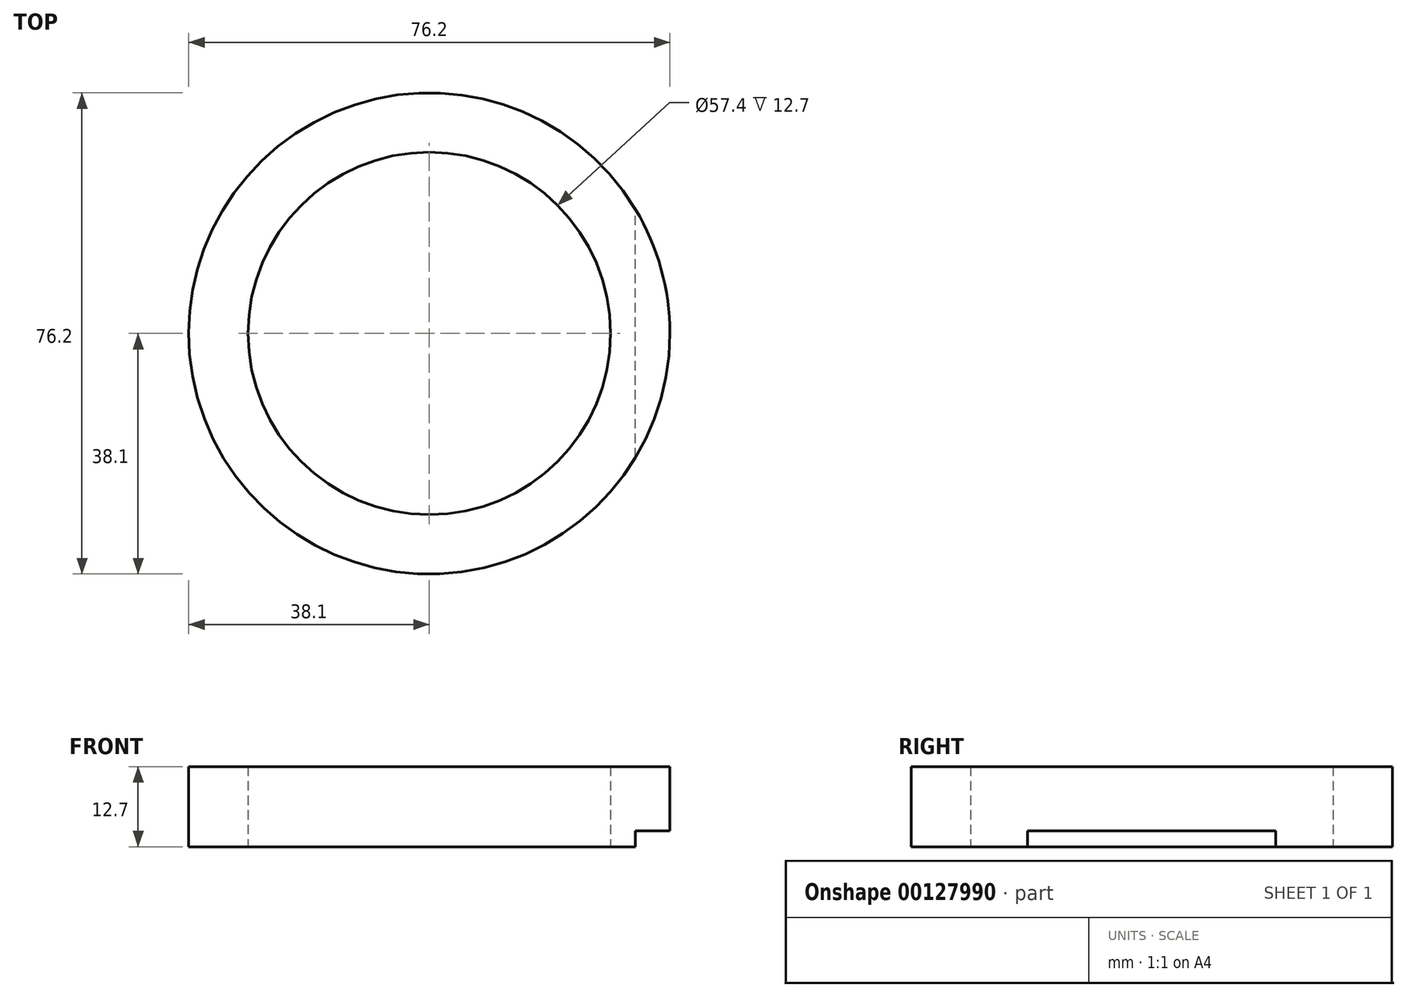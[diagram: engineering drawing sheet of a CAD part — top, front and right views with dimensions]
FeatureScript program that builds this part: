
annotation { "Feature Type Name" : "Feature", "Feature Type Description" : "" }
export const myFeature = defineFeature(function(context is Context, id is Id, definition is map)
    precondition{}
    {
        {
            var Q0;
            Q0=qCreatedBy(makeId("Top.planeOp"),FACE);
            var sketch = newSketch(context, id + "F0", { "sketchPlane" : qUnion([Q0])});
            skCircle(sketch, "E0", {"center": v(0, 0) * mm, "radius": 28.7 * mm});
            skCircle(sketch, "E1", {"center": v(0, 0) * mm, "radius": 38.1 * mm});
            skSolve(sketch);
        }
        {
            var Q0;
            Q0=makeQuery(id+"F0.imprint","IMPRINT",FACE,{"disambiguationData":[TD([[makeQuery(id+"F0.imprint","IMPRINT",EDGE,{"derivedFrom":sQuery(id+"F0.wireOp",EDGE,"E0")}),-1.0]])]});
            extrude(context, id + "F1", {"entities" : qUnion([Q0]), "depth" : 12.7 * mm});
        }
        {
            var Q0;
            Q0=makeQuery(id+"F1.opExtrude","CAP_FACE",FACE,{"disambiguationData":[OSD([sQuery(id+"F0.wireOp",EDGE,"E0"),sQuery(id+"F0.wireOp",EDGE,"E1")])],"isStart":true});
            var sketch = newSketch(context, id + "F2", { "sketchPlane" : qUnion([Q0])});
            skLineSegment(sketch, "E2.bottom", {"start": v(45.68, 39.57) * mm, "end": v(32.64, 39.57) * mm});
            skLineSegment(sketch, "E2.top", {"start": v(45.68, -36.96) * mm, "end": v(32.64, -36.96) * mm});
            skLineSegment(sketch, "E2.left", {"start": v(45.68, 39.57) * mm, "end": v(45.68, -36.96) * mm});
            skLineSegment(sketch, "E2.right", {"start": v(32.64, 39.57) * mm, "end": v(32.64, -36.96) * mm});
            skSolve(sketch);
        }
        {
            var Q0;
            {var subQ0=sQuery(id+"F2.wireOp",EDGE,"E2.right");var subQ1=makeQuery(id+"F1.opExtrude","CAP_EDGE",EDGE,{"disambiguationData":[OSD([sQuery(id+"F0.wireOp",EDGE,"E1")])],"isStart":true});var subQ2=makeQuery(id+"F2.imprint","INTERSECT",VERTEX,{"disambiguationData":[OD(0.0)],"derivedFrom":[subQ1,subQ0]});Q0=makeQuery(id+"F2.imprint","IMPRINT",FACE,{"disambiguationData":[TD([[makeQuery(id+"F2.imprint","IMPRINT",EDGE,{"disambiguationData":[TD([[subQ2,-1.0]])],"derivedFrom":subQ0}),1.0]])]});}
            var Q1;
            {var subQ1=sQuery(id+"F2.wireOp",EDGE,"E2.bottom");Q1=makeQuery(id+"F2.imprint","IMPRINT",FACE,{"disambiguationData":[TD([[makeQuery(id+"F2.imprint","IMPRINT",EDGE,{"derivedFrom":subQ1}),1.0]])]});}
            extrude(context, id + "F3", {"entities" : qUnion([Q0, Q1]), "operationType" : NewBodyOperationType.REMOVE, "oppositeDirection" : true, "depth" : 2.54 * mm});
        }
    });
